# Revit family: Baies d'extension Linkeo
name_source: partatom
category: Equipement spécialisé
units: mm (PartAtom-declared; Revit-internal decimal feet)

## family parameters
Basée sur le plan de construction = Non
Cote de connecteur circulaire = Utiliser le diamètre
Couper avec des vides une fois chargée = Non
Numéro OmniClass = 23.85.05.17.11.14
Partagée = Oui
Point de calcul de pièce = Non
Titre OmniClass = Multimedia Broadcasting Equipment
Toujours verticalement = Oui
Type d'élément = Normal

## types (1)
- Baie d'extension Linkeo2 42U 800x800
    Avec mise à la terre = Oui
    Avec porte frontale = Oui
    Avec tôle de toit = Oui
    Capacité de charge max = 400
    Classe d'application = EC002499
    Couleur = gris
    Dimension modulaire = 19 pouces
    Distance ouverture 1 = 257 mm  [stored 0.843176 ft]
    Distance ouverture 2 = 198 mm  [stored 0.649606 ft]
    EAN = 3414971001633
    Elévation par défaut = 0 mm  [stored 0 ft]
    Emplacement de rack = 93 mm  [stored 0.305118 ft]
    Fabricant = Legrand
    Finition de surface = Poudré
    Finition du rail profilé = Recourbée
    Fonction = Baie Linkeo2
    Hauteur = 2026 mm  [stored 6.64698 ft]
    Indice de protection IK = IK08
    Indice de protection IP = IP20
    Largeur (mm) = 810 mm
    Libellé BIM = Baie Linkeo2 42U 800x800
    Lien e-catalogue = https://www.legrand.fr
    Matériau = Acier
    Matériau de la porte avant = Verre
    Modèle = Corps fixe
    Modèle de largeur = 800 mm  [stored 2.62467 ft]
    Nombre d'unités en hauteur = 42
    Nombre de portes = 1
    Passage utile en hauteur (mm) = 1786 mm  [stored 5.85958 ft]
    Passage utile en largeur (mm) = 690 mm  [stored 2.26378 ft]
    Profondeur = 830 mm  [stored 2.7231 ft]
    Profondeur du modèle = 800 mm  [stored 2.62467 ft]
    RAL = 7016
    Référence Legrand = 646770
    Température de fonctionnement = -25°C à 70°C
    Température de stockage = -25°C à 70°C
    Type d'aération = Aucune
    Type de montage = Frontal
    Type de montants horizontaux = Montants horizontaux pour armoires Linkeo  42U profondeur 800
    Type de montants verticaux = Montants verticaux pour armoires Linkeo  42U
    Type de pieds de nivellement = Pieds de nivellement  800X800
    Verrouillage de la porte avant = A un point

note: [stored X ft] marks values corroborated as IEEE doubles in the binary element streams (Revit-internal decimal feet)
